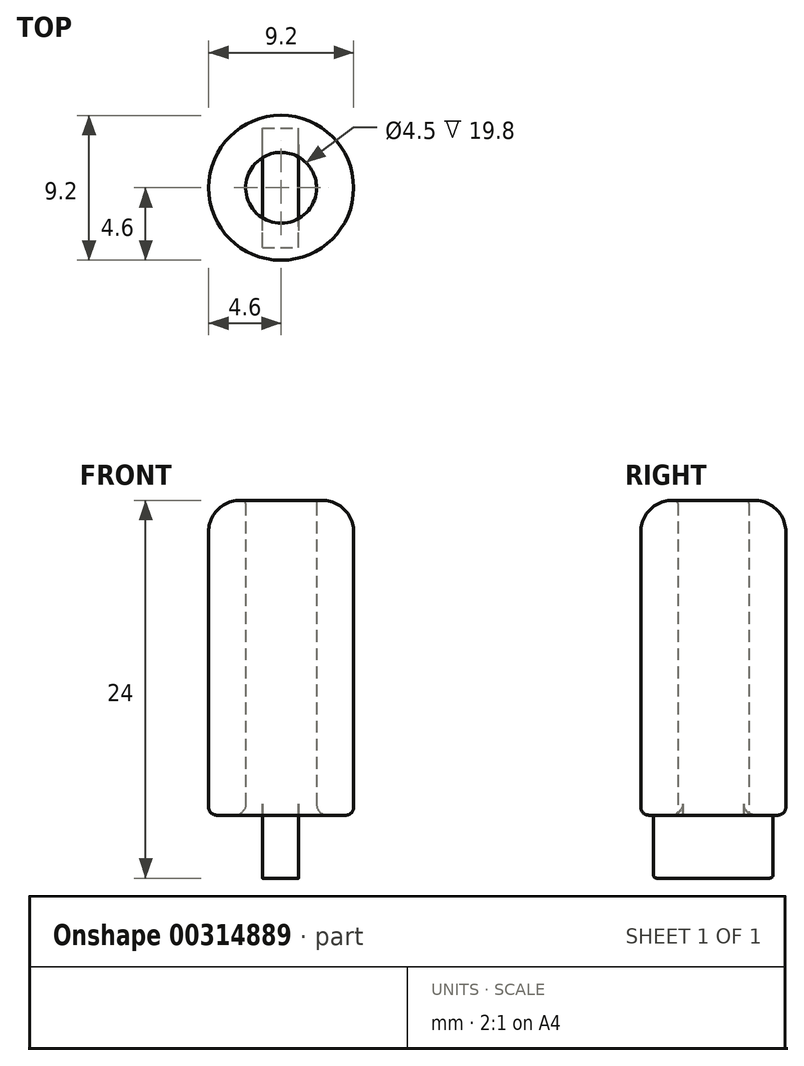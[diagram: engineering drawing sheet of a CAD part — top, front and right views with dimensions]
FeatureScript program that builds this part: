
annotation { "Feature Type Name" : "Feature", "Feature Type Description" : "" }
export const myFeature = defineFeature(function(context is Context, id is Id, definition is map)
    precondition{}
    {
        {
            var Q0;
            Q0=qCreatedBy(makeId("Top.planeOp"),FACE);
            var sketch = newSketch(context, id + "F0", { "sketchPlane" : qUnion([Q0])});
            skLineSegment(sketch, "E0.0", {"start": v(-3.5, -3) * mm, "end": v(3.5, -3) * mm});
            skLineSegment(sketch, "E1.0", {"start": v(-3.5, 3) * mm, "end": v(3.5, 3) * mm});
            skLineSegment(sketch, "E2.0", {"start": v(-3.5, 3) * mm, "end": v(-3.5, -3) * mm});
            skLineSegment(sketch, "E3.0", {"start": v(3.5, 3) * mm, "end": v(3.5, -3) * mm});
            skCircle(sketch, "E4", {"center": v(0, 0) * mm, "radius": 6 * mm});
            skCircle(sketch, "E5", {"center": v(0, 0) * mm, "radius": 1.75 * mm});
            skCircle(sketch, "E6.0", {"center": v(0, 0) * mm, "radius": 4.6 * mm});
            skSolve(sketch);
        }
        {
            var Q0;
            Q0=makeQuery(id+"F0.imprint","IMPRINT",FACE,{"disambiguationData":[TD([[makeQuery(id+"F0.imprint","IMPRINT",EDGE,{"derivedFrom":sQuery(id+"F0.wireOp",EDGE,"E4")}),1.0]])]});
            var Q1;
            {var subQ0=sQuery(id+"F0.wireOp",EDGE,"E6.0");var subQ1=sQuery(id+"F0.wireOp",EDGE,"E1.0");var subQ2=makeQuery(id+"F0.imprint","INTERSECT",VERTEX,{"disambiguationData":[OD(0.0)],"derivedFrom":[subQ1,subQ0]});Q1=makeQuery(id+"F0.imprint","IMPRINT",FACE,{"disambiguationData":[TD([[makeQuery(id+"F0.imprint","IMPRINT",EDGE,{"disambiguationData":[TD([[subQ2,-1.0]])],"derivedFrom":subQ1}),1.0]])]});}
            var Q2;
            {var subQ0=sQuery(id+"F0.wireOp",EDGE,"E6.0");var subQ1=sQuery(id+"F0.wireOp",EDGE,"E2.0");var subQ2=makeQuery(id+"F0.imprint","INTERSECT",VERTEX,{"disambiguationData":[OD(0.0)],"derivedFrom":[subQ1,subQ0]});Q2=makeQuery(id+"F0.imprint","IMPRINT",FACE,{"disambiguationData":[TD([[makeQuery(id+"F0.imprint","IMPRINT",EDGE,{"disambiguationData":[TD([[subQ2,-1.0]])],"derivedFrom":subQ1}),-1.0]])]});}
            var Q3;
            Q3=makeQuery(id+"F0.imprint","IMPRINT",FACE,{"disambiguationData":[TD([[makeQuery(id+"F0.imprint","IMPRINT",EDGE,{"derivedFrom":sQuery(id+"F0.wireOp",EDGE,"E5")}),-1.0]])]});
            var Q4;
            {var subQ0=sQuery(id+"F0.wireOp",EDGE,"E6.0");var subQ1=sQuery(id+"F0.wireOp",EDGE,"E0.0");var subQ2=makeQuery(id+"F0.imprint","INTERSECT",VERTEX,{"disambiguationData":[OD(0.0)],"derivedFrom":[subQ1,subQ0]});Q4=makeQuery(id+"F0.imprint","IMPRINT",FACE,{"disambiguationData":[TD([[makeQuery(id+"F0.imprint","IMPRINT",EDGE,{"disambiguationData":[TD([[subQ2,-1.0]])],"derivedFrom":subQ1}),-1.0]])]});}
            var Q5;
            {var subQ0=sQuery(id+"F0.wireOp",EDGE,"E6.0");var subQ1=sQuery(id+"F0.wireOp",EDGE,"E3.0");var subQ2=makeQuery(id+"F0.imprint","INTERSECT",VERTEX,{"disambiguationData":[OD(0.0)],"derivedFrom":[subQ1,subQ0]});Q5=makeQuery(id+"F0.imprint","IMPRINT",FACE,{"disambiguationData":[TD([[makeQuery(id+"F0.imprint","IMPRINT",EDGE,{"disambiguationData":[TD([[subQ2,-1.0]])],"derivedFrom":subQ1}),1.0]])]});}
            extrude(context, id + "F1", {"entities" : qUnion([Q0, Q1, Q2, Q3, Q4, Q5]), "depth" : 2 * mm});
        }
        {
            var Q0;
            Q0=makeQuery(id+"F0.imprint","IMPRINT",FACE,{"disambiguationData":[TD([[makeQuery(id+"F0.imprint","IMPRINT",EDGE,{"derivedFrom":sQuery(id+"F0.wireOp",EDGE,"E4")}),1.0]])]});
            extrude(context, id + "F2", {"entities" : qUnion([Q0]), "operationType" : NewBodyOperationType.ADD, "depth" : 14 * mm});
        }
        {
            var Q0;
            Q0=makeQuery(id+"F1.opExtrude","CAP_EDGE",EDGE,{"disambiguationData":[OSD([sQuery(id+"F0.wireOp",EDGE,"E4")])],"isStart":true});
            fillet(context, id + "F3", {"entities" : qUnion([Q0]), "radius" : 3.5 * mm, "tangentPropagation" : true, "allowEdgeOverflow" : false});
        }
        {
            var Q0;
            Q0=makeQuery(id+"F2.opExtrude","CAP_EDGE",EDGE,{"disambiguationData":[OSD([sQuery(id+"F0.wireOp",EDGE,"E4")])],"isStart":false});
            fillet(context, id + "F4", {"entities" : qUnion([Q0]), "radius" : 3.54 * mm, "tangentPropagation" : true, "allowEdgeOverflow" : false});
        }
        {
            var Q0;
            Q0=makeQuery(id+"F1.opExtrude","CAP_FACE",FACE,{"disambiguationData":[OSD([sQuery(id+"F0.wireOp",EDGE,"E0.0"),sQuery(id+"F0.wireOp",EDGE,"E1.0"),sQuery(id+"F0.wireOp",EDGE,"E2.0"),sQuery(id+"F0.wireOp",EDGE,"E3.0"),sQuery(id+"F0.wireOp",EDGE,"E4"),sQuery(id+"F0.wireOp",EDGE,"E5"),sQuery(id+"F0.wireOp",EDGE,"E6.0")])],"isStart":false});
            var sketch = newSketch(context, id + "F5", { "sketchPlane" : qUnion([Q0])});
            skCircle(sketch, "E7", {"center": v(0, 0) * mm, "radius": 4.6 * mm});
            skCircle(sketch, "E8", {"center": v(0, 0) * mm, "radius": 2.25 * mm});
            skSolve(sketch);
        }
        {
            var Q0;
            Q0 = qSketchRegion(id + "F5", true);
            extrude(context, id + "F6", {"entities" : qUnion([Q0]), "depth" : 40 * mm, "hasSecondDirection" : true, "secondDirectionOppositeDirection" : false, "secondDirectionDepth" : 20 * mm});
        }
        {
            var Q0;
            Q0=makeQuery(id+"F6.opExtrude","CAP_EDGE",EDGE,{"disambiguationData":[OSD([sQuery(id+"F5.wireOp",EDGE,"E7")])],"isStart":false});
            fillet(context, id + "F7", {"entities" : qUnion([Q0]), "radius" : 2 * mm, "tangentPropagation" : true, "allowEdgeOverflow" : false});
        }
        {
            var Q0;
            Q0=makeQuery(id+"F6.opExtrude","CAP_EDGE",EDGE,{"disambiguationData":[OSD([sQuery(id+"F5.wireOp",EDGE,"E7")])],"isStart":true});
            fillet(context, id + "F8", {"entities" : qUnion([Q0]), "radius" : 0.5 * mm, "tangentPropagation" : true, "allowEdgeOverflow" : false});
        }
        {
            var Q0;
            Q0=makeQuery(id+"F6.opExtrude","CAP_FACE",FACE,{"disambiguationData":[OSD([sQuery(id+"F5.wireOp",EDGE,"E7"),sQuery(id+"F5.wireOp",EDGE,"E8")])],"isStart":true});
            var sketch = newSketch(context, id + "F9", { "sketchPlane" : qUnion([Q0])});
            skLineSegment(sketch, "E9.bottom", {"start": v(-1.18, 3.8) * mm, "end": v(1.12, 3.8) * mm});
            skLineSegment(sketch, "E9.top", {"start": v(-1.18, -3.79) * mm, "end": v(1.12, -3.79) * mm});
            skLineSegment(sketch, "E9.right", {"start": v(1.12, 3.8) * mm, "end": v(1.12, -3.79) * mm});
            skLineSegment(sketch, "E10", {"start": v(-1.18, 3.8) * mm, "end": v(-1.18, -3.79) * mm});
            skSolve(sketch);
        }
        {
            var Q0;
            Q0 = qSketchRegion(id + "F9", true);
            extrude(context, id + "F10", {"entities" : qUnion([Q0]), "operationType" : NewBodyOperationType.ADD, "depth" : 4 * mm});
        }
        {
            var Q0;
            {var subQ0=sQuery(id+"F5.wireOp",EDGE,"E8");var subQ1=makeQuery(id+"F6.opExtrude","CAP_FACE",FACE,{"disambiguationData":[OSD([sQuery(id+"F5.wireOp",EDGE,"E7"),subQ0])],"isStart":true});var subQ2=sQuery(id+"F9.wireOp",EDGE,"E9.right");var subQ3=makeQuery(id+"F6.opExtrude","SWEPT_FACE",FACE,{"disambiguationData":[OSD([subQ0])]});Q0=makeQuery(id+"F10.boolean.opBoolean","SPLIT",EDGE,{"disambiguationData":[topologyDisambiguationEdgeConnected([subQ1,subQ3]),TD([makeQuery(id+"F10.opExtrude","SWEPT_FACE",FACE,{"disambiguationData":[OSD([subQ2])]})])],"derivedFrom":makeQuery(id+"F6.opExtrude","CAP_EDGE",EDGE,{"disambiguationData":[OSD([subQ0])],"isStart":true})});}
            var Q1;
            {var subQ0=sQuery(id+"F5.wireOp",EDGE,"E8");var subQ1=makeQuery(id+"F6.opExtrude","CAP_FACE",FACE,{"disambiguationData":[OSD([sQuery(id+"F5.wireOp",EDGE,"E7"),subQ0])],"isStart":true});var subQ2=sQuery(id+"F9.wireOp",EDGE,"E10");var subQ3=makeQuery(id+"F6.opExtrude","SWEPT_FACE",FACE,{"disambiguationData":[OSD([subQ0])]});Q1=makeQuery(id+"F10.boolean.opBoolean","SPLIT",EDGE,{"disambiguationData":[topologyDisambiguationEdgeConnected([subQ1,subQ3]),TD([makeQuery(id+"F10.opExtrude","SWEPT_FACE",FACE,{"disambiguationData":[OSD([subQ2])]})])],"derivedFrom":makeQuery(id+"F6.opExtrude","CAP_EDGE",EDGE,{"disambiguationData":[OSD([subQ0])],"isStart":true})});}
            fillet(context, id + "F11", {"entities" : qUnion([Q0, Q1]), "radius" : 0.7 * mm, "tangentPropagation" : true, "allowEdgeOverflow" : false});
        }
        {
            var Q0;
            Q0=makeQuery(id+"F6.opExtrude","CAP_EDGE",EDGE,{"disambiguationData":[OSD([sQuery(id+"F5.wireOp",EDGE,"E8")])],"isStart":false});
            var Q1;
            Q1=makeQuery(id+"F10.opExtrude","CAP_EDGE",EDGE,{"disambiguationData":[OSD([sQuery(id+"F9.wireOp",EDGE,"E9.bottom")])],"isStart":false});
            var Q2;
            Q2=makeQuery(id+"F10.opExtrude","CAP_EDGE",EDGE,{"disambiguationData":[OSD([sQuery(id+"F9.wireOp",EDGE,"E9.top")])],"isStart":false});
            fillet(context, id + "F12", {"entities" : qUnion([Q0, Q1, Q2]), "radius" : 0.2 * mm, "tangentPropagation" : true, "allowEdgeOverflow" : false});
        }
    });
